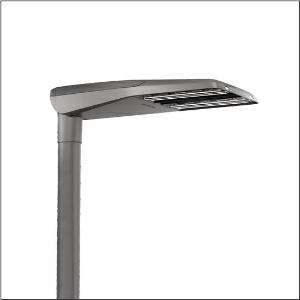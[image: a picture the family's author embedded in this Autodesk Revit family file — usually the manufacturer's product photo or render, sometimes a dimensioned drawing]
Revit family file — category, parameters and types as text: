
# Revit family: streetlight_sl_11_iq_midi___st1_2p1_0_5xc3g41f08me_0c33
name_source: partatom
category: Lighting Fixtures
units: mm (PartAtom-declared; Revit-internal decimal feet)

## family parameters
Cut with Voids When Loaded = No
Host = Face
Light Source = No
Part Type = Normal
Room Calculation Point = No
Round Connector Dimension = Use Diameter
Shared = No

## types (1)
- --- (1 x LED, 18520 lm, 124.7 W, 4000K)
    Apparent Load = 125 VA
    CIE Flux Codes = 31 68 95 100 100
    Color Rendering = 70
    Color Temperature = 4000K
    Default Elevation = 1800 mm
    Description = Streetlight SL 11 iQ midi, mast luminaire, primary light control with 3 zone facetted reflector, of plastic, silver coated, highly specular, primary optical cover: cover, of PMMA, transparent, light distribution: ST1.2P1.0, light emission: direct distribution, primary light characteristic: asymmetric, installation type: post-top, side-entry, LED, High Power LED, rated luminous flux: 18.520lm, luminous efficacy: 149lm/W, light colour: 740, colour temperature: 4000K, control: Street-Remote, optimised constant luminous flux control (CLO 2.0), Auto-Match, Desk-Remote (wireless, voltage-free reading and setting of iQ features in the workshop via application-optimized NFC function/RFID function), Light-Fading, Smart-Wire, Night-Set, Lumen-Switch, Temp-Guard, with cable H07RN-F 5x 1.5mm², mains connection: 230..240V, AC, 50/60Hz, connection cable pre-assembled, cable length: 12,5m, start of lifetime: 125W, end of service life: 132W, reduction: 57W, luminaire housing, of diecast aluminium, powder-coated, Siteco® metallic grey (DB 702S), please order mast flange separately, inclination adjustable without tools: 0°, 5°, 10°, 15° (post-top) | 0°, -5°, -10°, -15° (side-entry), sealing non-destructively replaceable, multi-level sealing system, length: 780mm, width: 376mm, height: 118mm, mast flange for spigot size: 42mm (side-entry): 5XC10008XM4, 60/48mm (side-entry/post-top): 5XC10108XM2, 76/60mm (side-entry/post-top): 5XC10108XM1, equipment: Power, protection rating (complete): IP66, insulation class (complete): insulation class II (safety insulation), certification: CE, ENEC, VDE, impact resistance: IK09, permissible operating ambient temperature for outdoor applications: -25..+50°C, standard-compliant lighting for roads and squares, Environmental Product Declaration (EPD) tested and certified by an independent institute, packaging unit: 1 piece

Light Distribution: ST1.2P1.0
    Height = 118 mm
    Lamp = 1 x LED
    Lamp Light Flux = 18520 lm
    Lamp Power = 124.7 W
    Lamp count = 1
    Length = 780 mm
    Luminous efficacy = 149 lm/W
    Manufacturer = Siteco
    ModVariant = No
    Model = 5XC3G41F08ME
    Number of Poles = 1
    OnlyDefault = Yes
    Power Factor = 1
    Product Name = Streetlight SL 11 iQ midi | ST1.2P1.0
    Product group = mast luminaire | pylon top
    ProductGroupID = 6100
    Protection Class = Protection class II
    Protection Degree = IP 66
    RLX_Detail_Level = 1
    RLX_Emergency_Light_Flux = 0 lm
    RLX_Emergency_Type = 0
    RLX_Emergency_Type_DB = No
    RlxData = <blob elided: 70677 chars, md5=1ab37e30>
    Socket = socket
    Standby Power = 0 W
    System Light Flux = 18520 lm
    System Power = 125 W
    Type Comments = factory setting: luminous flux: 100 % | dim-lin: 254 | 557 mA
    Type Image = l_1005960.jpg
    URL = http://relux.com
    VarID = @adj_147579
    Voltage = 0 V
    Weight = 0.00 kg
    Width = 376 mm

## geometry (parser evidence)
native form markers: Blend x4, Sweep x10
no freeform markers — native parametric forms only
